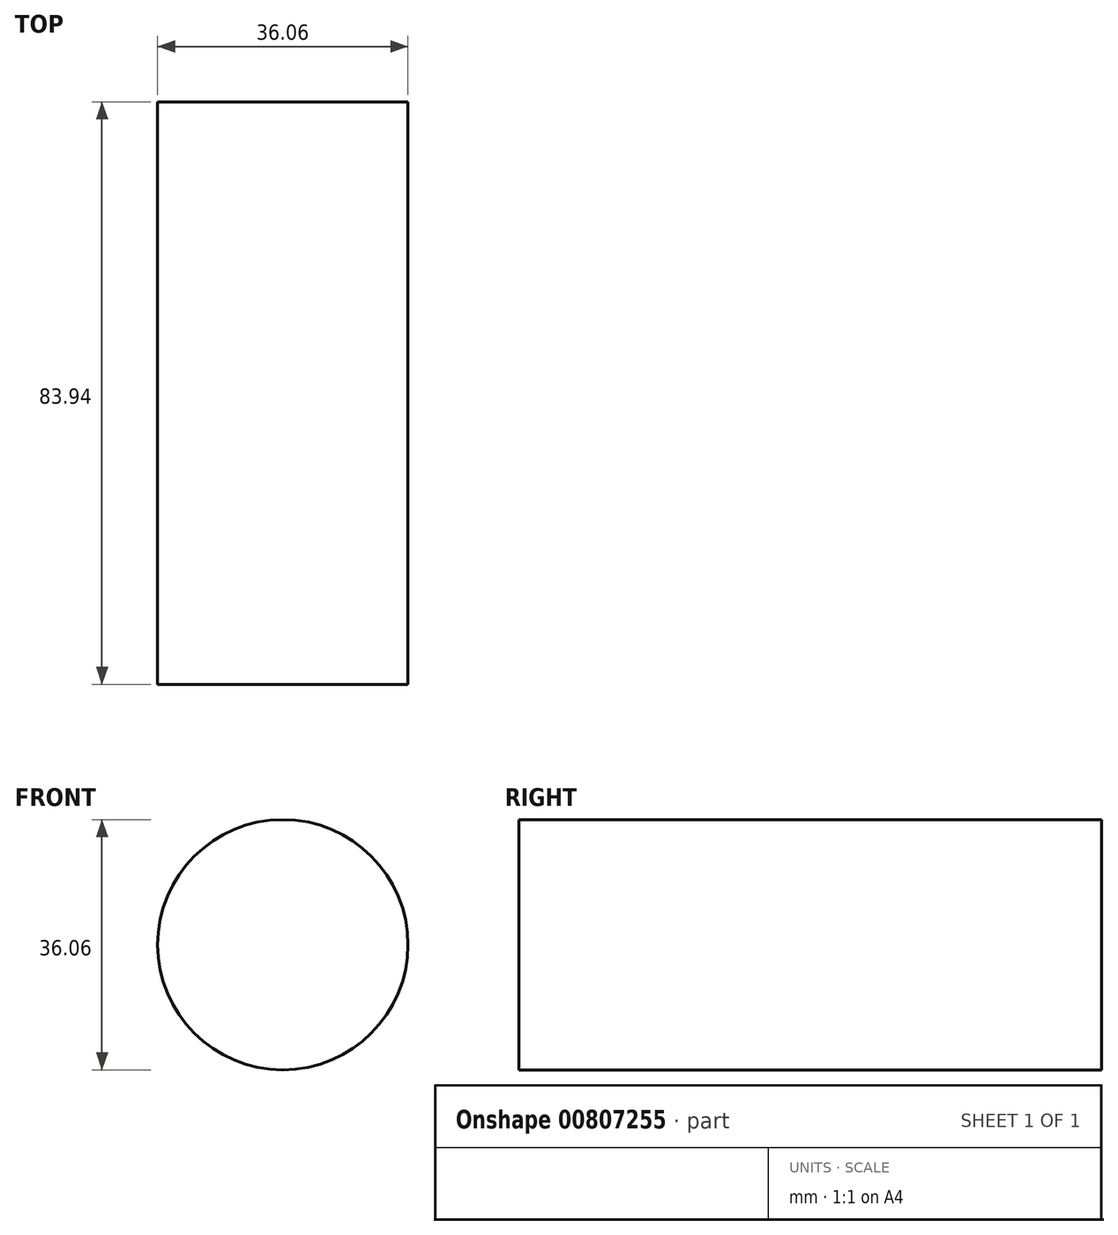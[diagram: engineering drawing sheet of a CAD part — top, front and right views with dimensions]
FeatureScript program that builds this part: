
annotation { "Feature Type Name" : "Feature", "Feature Type Description" : "" }
export const myFeature = defineFeature(function(context is Context, id is Id, definition is map)
    precondition{}
    {
        {
            var Q0;
            Q0=qCreatedBy(makeId("Front.planeOp"),FACE);
            var sketch = newSketch(context, id + "F0", { "sketchPlane" : qUnion([Q0])});
            skCircle(sketch, "E0", {"center": v(0, 54.17) * mm, "radius": 18.03 * mm});
            skSolve(sketch);
        }
        {
            var Q0;
            Q0=makeQuery(id+"F0.imprint","IMPRINT",FACE,{"disambiguationData":[TD([[makeQuery(id+"F0.imprint","IMPRINT",EDGE,{"derivedFrom":sQuery(id+"F0.wireOp",EDGE,"E0")}),1.0]])]});
            extrude(context, id + "F1", {"entities" : qUnion([Q0]), "depth" : 83.94 * mm, "offsetDistance" : 25 * mm});
        }
    });
